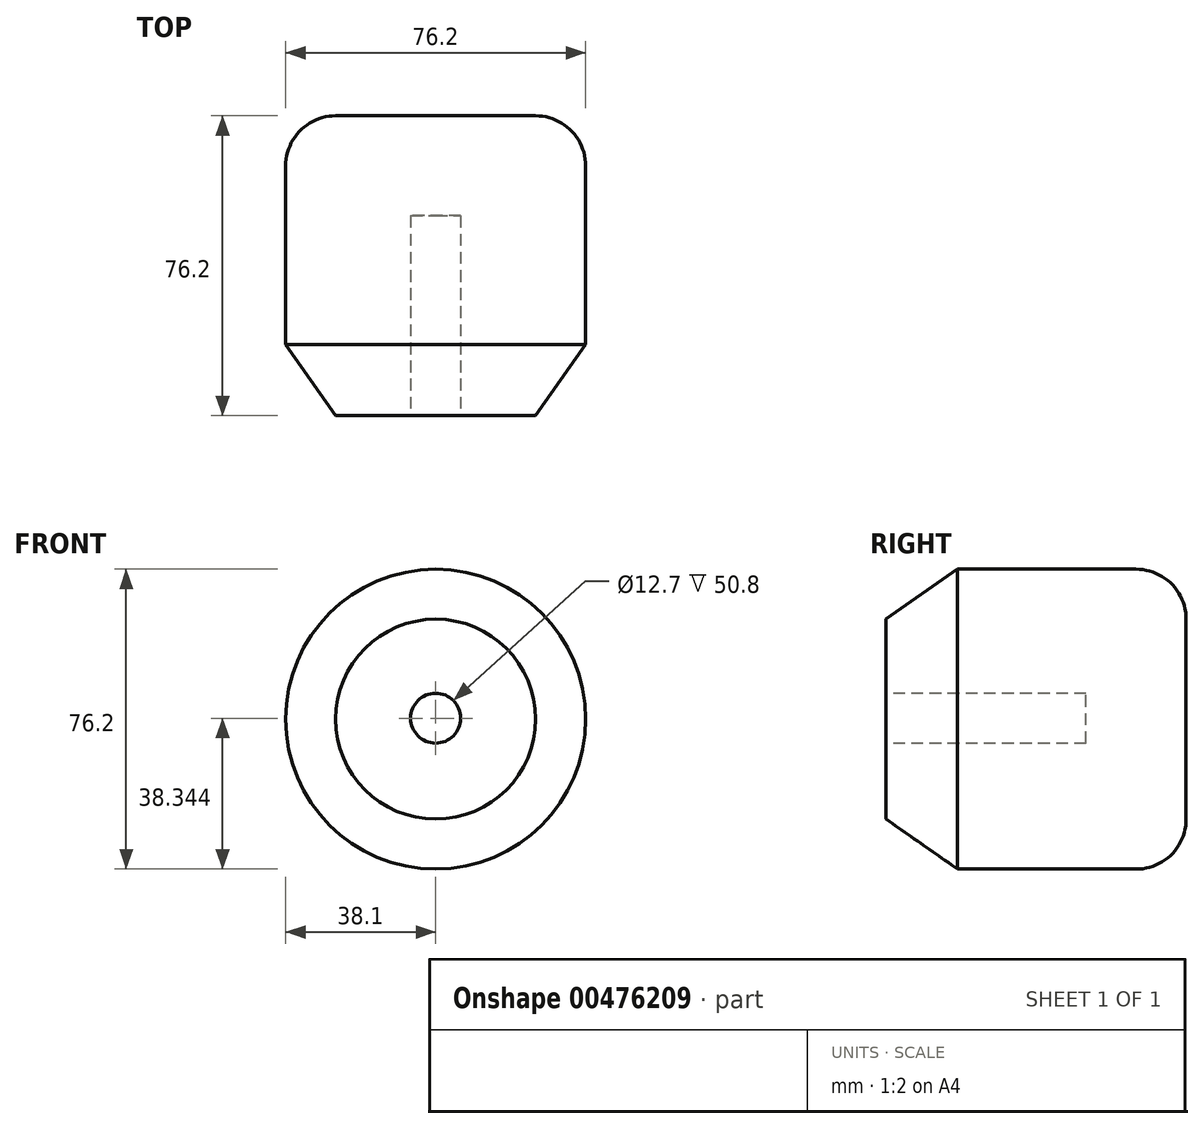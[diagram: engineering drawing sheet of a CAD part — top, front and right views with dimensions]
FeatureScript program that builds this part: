
annotation { "Feature Type Name" : "Feature", "Feature Type Description" : "" }
export const myFeature = defineFeature(function(context is Context, id is Id, definition is map)
    precondition{}
    {
        {
            var Q0;
            Q0=qCreatedBy(makeId("Front.planeOp"),FACE);
            var sketch = newSketch(context, id + "F0", { "sketchPlane" : qUnion([Q0])});
            skCircle(sketch, "E0", {"center": v(0, 0) * mm, "radius": 38.1 * mm});
            skSolve(sketch);
        }
        {
            var Q0;
            Q0 = qSketchRegion(id + "F0", true);
            extrude(context, id + "F1", {"entities" : qUnion([Q0]), "depth" : 76.2 * mm});
        }
        {
            var Q0;
            Q0=makeQuery(id+"F1.opExtrude","CAP_EDGE",EDGE,{"disambiguationData":[OSD([sQuery(id+"F0.wireOp",EDGE,"E0")])],"isStart":true});
            fillet(context, id + "F2", {"entities" : qUnion([Q0]), "radius" : 12.7 * mm, "tangentPropagation" : true, "allowEdgeOverflow" : false});
        }
        {
            var Q0;
            Q0=makeQuery(id+"F1.opExtrude","CAP_FACE",FACE,{"disambiguationData":[OSD([sQuery(id+"F0.wireOp",EDGE,"E0"),sQuery(id+"F0.wireOp",EDGE,"p3vSmcsO-SNkw-wali-FWRK-FnZvN2fkpERY")])],"isStart":false});
            var sketch = newSketch(context, id + "F3", { "sketchPlane" : qUnion([Q0])});
            skCircle(sketch, "E1", {"center": v(0, 0.24) * mm, "radius": 6.35 * mm});
            skSolve(sketch);
        }
        {
            var Q0;
            Q0 = qSketchRegion(id + "F3", true);
            extrude(context, id + "F4", {"entities" : qUnion([Q0]), "operationType" : NewBodyOperationType.REMOVE, "oppositeDirection" : true, "depth" : 50.8 * mm});
        }
        {
            var Q0;
            Q0=makeQuery(id+"F1.opExtrude","CAP_EDGE",EDGE,{"disambiguationData":[OSD([sQuery(id+"F0.wireOp",EDGE,"E0")])],"isStart":false});
            chamfer(context, id + "F5", {"entities" : qUnion([Q0]), "chamferType" : ChamferType.OFFSET_ANGLE, "width" : 12.7 * mm, "oppositeDirection" : false, "angle" : 55 * degree, "tangentPropagation" : true});
        }
    });
